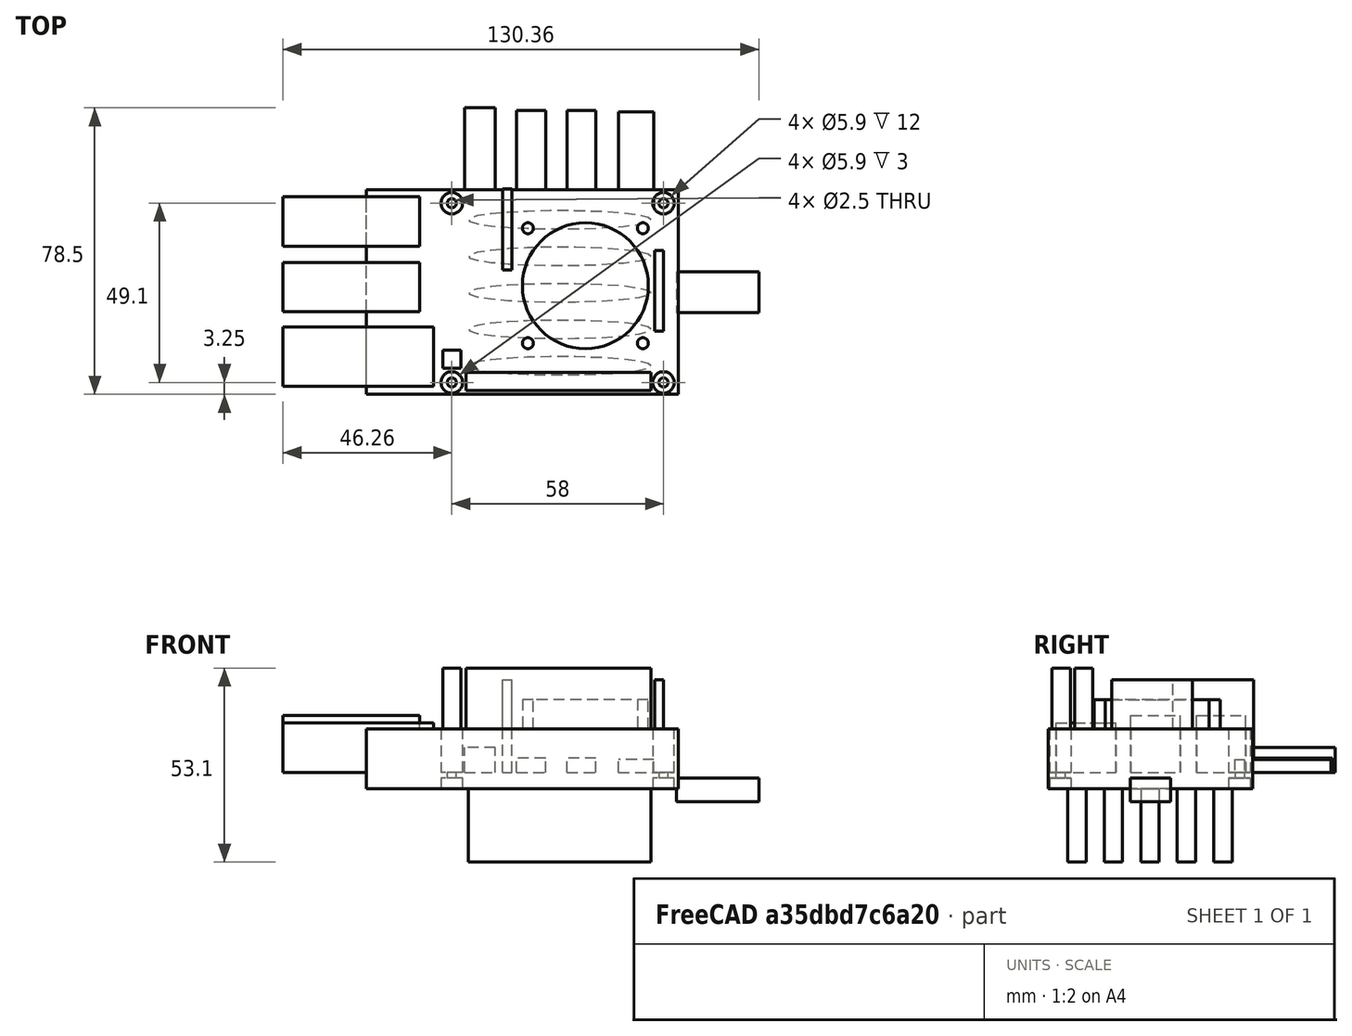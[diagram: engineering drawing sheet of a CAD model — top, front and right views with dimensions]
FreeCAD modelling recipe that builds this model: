
FCSTD DOCUMENT  (FreeCAD 0.21R33771 (Git))
Label: rpi_negative
License: All rights reserved
LicenseURL: http://en.wikipedia.org/wiki/All_rights_reserved
objects: Part::Box×17, Part::Cylinder×13, Part::MultiFuse×3, Part::Cut×2, Part::Feature×1, Part::Fuse×1
note: 37 computed .brp shape members not serialized (recipe doc carries the construction recipe); baked Part::Feature solids carry a one-line shape summary decoded from their .brp

FEATURE [Part::Box] cube
  AttacherType = Attacher::AttachEngine3D
  Height = 1.5
  Length = 85.5
  Placement = pos=(0,0,-1.5) rot=(0,0,1;0rad)
  Width = 56
FEATURE [Part::Box] cube001
  AttacherType = Attacher::AttachEngine3D
  Height = 13.6
  Length = 41.3
  Placement = pos=(-22.81,2.15,0) rot=(0,0,1;0rad)
  Width = 16.3
FEATURE [Part::Box] cube002
  AttacherType = Attacher::AttachEngine3D
  Height = 15.6
  Length = 37.44
  Placement = pos=(-22.81,22.6,0) rot=(0,0,1;0rad)
  Width = 13.5
FEATURE [Part::Box] cube003
  AttacherType = Attacher::AttachEngine3D
  Height = 15.6
  Length = 37.44
  Placement = pos=(-22.81,40.6,0) rot=(0,0,1;0rad)
  Width = 13.5
FEATURE [Part::Box] cube004
  AttacherType = Attacher::AttachEngine3D
  Height = 28.6
  Length = 50.7
  Placement = pos=(27.36,1,0) rot=(0,0,1;0rad)
  Width = 5
FEATURE [Part::Box] cube005
  AttacherType = Attacher::AttachEngine3D
  Height = 28.6
  Length = 5
  Placement = pos=(21,7.15,0) rot=(0,0,1;0rad)
  Width = 5
FEATURE [Part::Box] cube006
  AttacherType = Attacher::AttachEngine3D
  Height = 2.5
  Length = 15
  Placement = pos=(48,16.3,0) rot=(0,0,1;0rad)
  Width = 15
FEATURE [Part::Box] cube007
  AttacherType = Attacher::AttachEngine3D
  Height = 1.8
  Length = 10.8
  Placement = pos=(67.5,6.8,0) rot=(0,0,1;0rad)
  Width = 13.1
FEATURE [Part::Box] cube008
  AttacherType = Attacher::AttachEngine3D
  Height = 25.4
  Length = 2.5
  Placement = pos=(79,17.3,0) rot=(0,0,1;0rad)
  Width = 22.15
FEATURE [Part::Box] cube009
  AttacherType = Attacher::AttachEngine3D
  Height = 3.6
  Length = 9.7
  Placement = pos=(69.1,50,0) rot=(0,0,1;0rad)
  Width = 27.4
FEATURE [Part::Box] cube010
  AttacherType = Attacher::AttachEngine3D
  Height = 3.9
  Length = 7.95
  Placement = pos=(55,50,0) rot=(0,0,1;0rad)
  Width = 27.8
FEATURE [Part::Box] cube011
  AttacherType = Attacher::AttachEngine3D
  Height = 3.9
  Length = 7.95
  Placement = pos=(41.2,50,0) rot=(0,0,1;0rad)
  Width = 27.8
FEATURE [Part::Box] cube012
  AttacherType = Attacher::AttachEngine3D
  Height = 25.4
  Length = 2.5
  Placement = pos=(37.4,34.1,0) rot=(0,0,1;0rad)
  Width = 22.15
FEATURE [Part::Box] cube013
  AttacherType = Attacher::AttachEngine3D
  Height = 6.9
  Length = 8.5
  Placement = pos=(26.9,43.55,0) rot=(0,0,1;0rad)
  Width = 34.95
FEATURE [Part::Box] cube014
  AttacherType = Attacher::AttachEngine3D
  Height = 6.5
  Length = 22.55
  Placement = pos=(85,22.4,-8) rot=(0,0,1;0rad)
  Width = 11.11
FEATURE [Part::Cylinder] cylinder
  Angle = 360
  AttacherType = Attacher::AttachEngine3D
  FirstAngle = 0
  Height = 20
  Placement = pos=(44.3,14,0) rot=(0,0,1;0rad)
  Radius = 1.5
  SecondAngle = 0
FEATURE [Part::Cylinder] cylinder001
  Angle = 360
  AttacherType = Attacher::AttachEngine3D
  FirstAngle = 0
  Height = 20
  Placement = pos=(44.3,45.5,0) rot=(0,0,1;0rad)
  Radius = 1.5
  SecondAngle = 0
FEATURE [Part::Cylinder] cylinder002
  Angle = 360
  AttacherType = Attacher::AttachEngine3D
  FirstAngle = 0
  Height = 20
  Placement = pos=(75.8,14,0) rot=(0,0,1;0rad)
  Radius = 1.5
  SecondAngle = 0
FEATURE [Part::Cylinder] cylinder003
  Angle = 360
  AttacherType = Attacher::AttachEngine3D
  FirstAngle = 0
  Height = 20
  Placement = pos=(75.8,45.5,0) rot=(0,0,1;0rad)
  Radius = 1.5
  SecondAngle = 0
FEATURE [Part::Cylinder] cylinder004
  Angle = 360
  AttacherType = Attacher::AttachEngine3D
  FirstAngle = 0
  Height = 20
  Placement = pos=(60.05,29.75,0) rot=(0,0,1;0rad)
  Radius = 17.25
  SecondAngle = 0
FEATURE [Part::Feature] Matrix_Deformation
  Placement = pos=(53,7.8,0) rot=(0,0,1;0rad)
  shape: bbox 75 x 48.66 x 20 mm, 15 faces, 5 solids (baked)
FEATURE [Part::Box] cube015
  AttacherType = Attacher::AttachEngine3D
  Height = 12
  Length = 85.5
  Width = 56
FEATURE [Part::Box] cube016
  AttacherType = Attacher::AttachEngine3D
  Height = 3
  Length = 85.5
  Placement = pos=(0,0,-4.5) rot=(0,0,1;0rad)
  Width = 56
FEATURE [Part::Fuse] union
  Base = -> cube015
  Tool = -> cube016
FEATURE [Part::Cylinder] cylinder010
  Angle = 360
  AttacherType = Attacher::AttachEngine3D
  FirstAngle = 0
  Height = 22
  Placement = pos=(22.2,2,-11) rot=(0,0,1;0rad)
  Radius = 2.95
  SecondAngle = 0
FEATURE [Part::Cylinder] cylinder011
  Angle = 360
  AttacherType = Attacher::AttachEngine3D
  FirstAngle = 0
  Height = 22
  Placement = pos=(22.2,51.1,-11) rot=(0,0,1;0rad)
  Radius = 2.95
  SecondAngle = 0
FEATURE [Part::Cylinder] cylinder012
  Angle = 360
  AttacherType = Attacher::AttachEngine3D
  FirstAngle = 0
  Height = 22
  Placement = pos=(80.2,2,-11) rot=(0,0,1;0rad)
  Radius = 2.95
  SecondAngle = 0
FEATURE [Part::Cylinder] cylinder013
  Angle = 360
  AttacherType = Attacher::AttachEngine3D
  FirstAngle = 0
  Height = 22
  Placement = pos=(80.2,51.1,-11) rot=(0,0,1;0rad)
  Radius = 2.95
  SecondAngle = 0
FEATURE [Part::MultiFuse] Matrix_Union001
  Placement = pos=(1.25,1.25,4.5) rot=(0,0,1;0rad)
  Shapes = -> [cylinder010,cylinder011,cylinder012,cylinder013]
FEATURE [Part::Cut] difference
  Base = -> union
  Tool = -> Matrix_Union001
FEATURE [Part::MultiFuse] Matrix_Union002
  Placement = pos=(0,0,1.5) rot=(0,0,1;0rad)
  Shapes = -> [cube,cube001,cube002,cube003,cube004,cube005,cube006,cube007,cube008,cube009,cube010,cube011,cube012,cube013,cube014,cylinder,cylinder001,cylinder002,cylinder003,cylinder004,Matrix_Deformation,difference]
FEATURE [Part::Cylinder] cylinder014
  Angle = 360
  AttacherType = Attacher::AttachEngine3D
  FirstAngle = 0
  Height = 22
  Placement = pos=(22.2,2,-11) rot=(0,0,1;0rad)
  Radius = 1.25
  SecondAngle = 0
FEATURE [Part::Cylinder] cylinder015
  Angle = 360
  AttacherType = Attacher::AttachEngine3D
  FirstAngle = 0
  Height = 22
  Placement = pos=(22.2,51.1,-11) rot=(0,0,1;0rad)
  Radius = 1.25
  SecondAngle = 0
FEATURE [Part::Cylinder] cylinder016
  Angle = 360
  AttacherType = Attacher::AttachEngine3D
  FirstAngle = 0
  Height = 22
  Placement = pos=(80.2,2,-11) rot=(0,0,1;0rad)
  Radius = 1.25
  SecondAngle = 0
FEATURE [Part::Cylinder] cylinder017
  Angle = 360
  AttacherType = Attacher::AttachEngine3D
  FirstAngle = 0
  Height = 22
  Placement = pos=(80.2,51.1,-11) rot=(0,0,1;0rad)
  Radius = 1.25
  SecondAngle = 0
FEATURE [Part::MultiFuse] Matrix_Union003
  Placement = pos=(1.25,1.25,4.5) rot=(0,0,1;0rad)
  Shapes = -> [cylinder014,cylinder015,cylinder016,cylinder017]
FEATURE [Part::Cut] difference001
  Base = -> Matrix_Union002
  Placement = pos=(37.44,65,0) rot=(0,0,1;0rad)
  Tool = -> Matrix_Union003
